# Revit family: 0039738
name_source: partatom
category: Lighting Fixtures
revit_build: Autodesk Revit 2018 (Build: 20170223_1515(x64)
units: mm (PartAtom-declared; Revit-internal decimal feet)

## family parameters
Cut with Voids When Loaded = No
Host = Face
Light Source = Yes
OmniClass Number = 23.80.70.00
OmniClass Title = Lighting
Part Type = Normal
Room Calculation Point = No
Round Connector Dimension = Use Diameter
Shared = No

## types (1)
- 0039738 GRANIT IP65 0-10V 26000LM 865 WB
    Apparent Load = 0 VA
    Assembly Code = D5020200
    AssetType = Fixed
    ClassificationName = Uniclass2015
    ClassificationValue = EF_70_80
    Color Filter = 16777215
    Cost = 0 $
    Default Elevation = 1219 mm
    Dimming Lamp Color Temperature Shift = <None>
    DocumentationLiterature = http://www.sylvania-lighting.com
    Emit Shape Visible in Rendering = No
    Emit from Circle Diameter = 610 mm
    IfcExportType = IfcLightFixtureType
    ImpactProtectionIndex = IfcLightFixtureType
    IngressProtection = IfcLightFixtureType
    InputVoltage = 0
    LampColourRenderingIndex = 16500
    LampColourTemperature = LED
    LightOutputRatio = LED
    LuminaireType = 0
    Material = Feilo Sylvania
    Material_1_SYL = <By Category>
    Material_2_SYL = <By Category>
    Material_3_SYL = <By Category>
    Material_4_SYL = <By Category>
    Model = Granit IP65 0-10V 26000lm 865 WB
    ModelNumber = 0039738
    ModelReference = Granit IP65 0-10V 26000lm 865 WB
    Name = Granit IP65 0-10V 26000lm 865 WB
    NominalDepth = 370 mm  [stored 1.21391 ft]
    NominalHeight = 163 mm  [stored 0.534777 ft]
    NominalLength = 370 mm  [stored 1.21391 ft]
    Photometric Web File = 0039738.IES
    PowerConsumption = Lighting
    PowerFactor = 0
    Tilt Angle = -90.00°
    Type Image = <None>
    TypeName = Granit IP65 0-10V 26000lm 865 WB
    URL = 0
    Voltage = 0 V
    WarrantyDescription = http://www.sylvania-lighting.com

note: [stored X ft] marks values corroborated as IEEE doubles in the binary element streams (Revit-internal decimal feet)

## geometry (parser evidence)
native form markers: Sweep x1
no freeform markers — native parametric forms only
